# Revit family: FP_Revit_18_VB24SDEX1_Vacuum_Drawer_90001828A
name_source: partatom
category: Specialty Equipment
revit_build: Autodesk Revit 2018 (Build: 20170223_1515(x64)
units: mm (PartAtom-declared; Revit-internal decimal feet)

## family parameters
Always vertical = Yes
Cut with Voids When Loaded = Yes
OmniClass Number = 23.40.40.00
OmniClass Title = Food Service Equipment and Furnishings
Part Type = Normal
Room Calculation Point = No
Round Connector Dimension = Use Diameter
Shared = No
Work Plane-Based = No

## types (1)
- VB24SDEX1
    Cavity - Depth = 550 mm
    Cavity - Height = 142 mm  [stored 0.465879 ft]
    Cavity - Width = 560 mm
    Chassis - Depth = 545 mm  [stored 1.78806 ft]
    Chassis - Height = 140 mm  [stored 0.459318 ft]
    Chassis - Width = 543 mm  [stored 1.7815 ft]
    Connector Description - Electrical = 110 V, 60 Hz, 10 A
    Description = 24" Vacuum Drawer
    Manufacturer = Fisher & Paykel Appliances
    Material - Body = Fisher & Paykel - Grey
    Material - Door Front = Fisher & Paykel - Stainless Steel
    Material - Glass = Fisher & Paykel - Glass, Black
    Material - Structure = Fisher & Paykel - Black
    Material - Trim = Fisher & Paykel - Black
    Model = VB24SDEX1
    Product - Depth = 567 mm
    Product - Height = 140 mm  [stored 0.459318 ft]
    Product - Width = 596 mm  [stored 1.95538 ft]
    URL = www.fisherpaykel.com
    Visibility - Clearance Required = Yes

note: [stored X ft] marks values corroborated as IEEE doubles in the binary element streams (Revit-internal decimal feet)

## geometry (parser evidence)
native form markers: Sweep x5
no freeform markers — native parametric forms only
